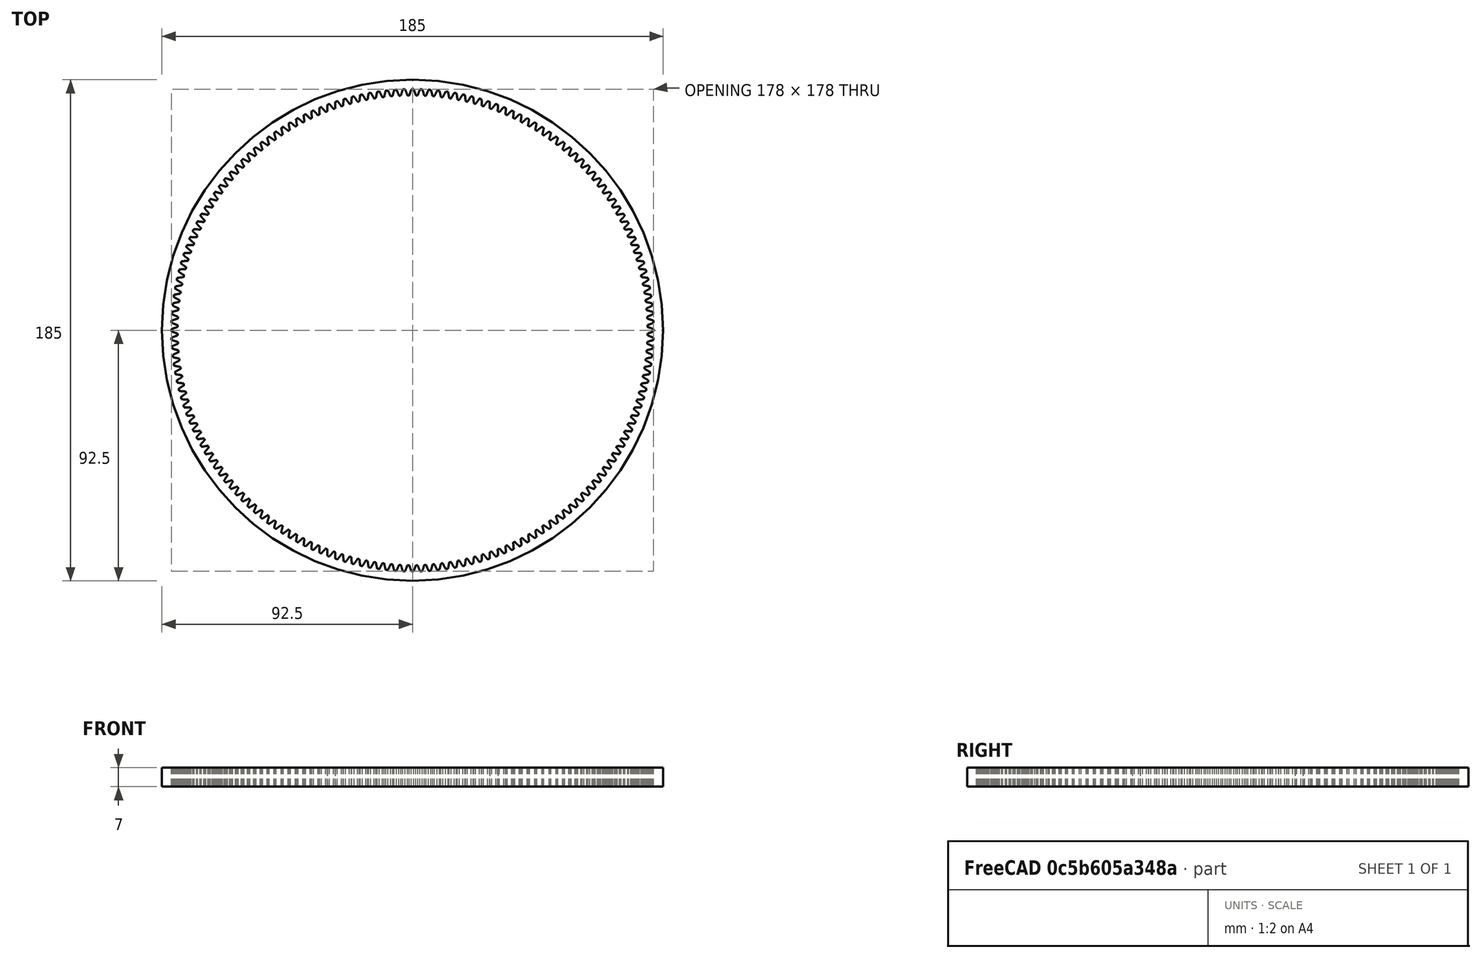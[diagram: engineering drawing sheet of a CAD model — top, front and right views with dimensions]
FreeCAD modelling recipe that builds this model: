
FCSTD DOCUMENT  (FreeCAD 0.19R24276 (Git))
Label: In_gear_t176_w7_cat_d185
License: All rights reserved
LicenseURL: http://en.wikipedia.org/wiki/All_rights_reserved
objects: PartDesign::FeaturePython×1, PartDesign::Body×1, Part::Cylinder×1, Part::Cut×1
note: 4 computed .brp shape members not serialized (recipe doc carries the construction recipe); baked Part::Feature solids carry a one-line shape summary decoded from their .brp

FEATURE [PartDesign::FeaturePython] involutegear001  # WARN: FeaturePython — macro-defined, semantics opaque (R4)
  AttacherType = Attacher::AttachEngine3D
  backlash = 0
  beta = 0
  clearance = 0.25
  da = 178
  df = 173.5
  double_helix = false
  dw = 176
  head = 0
  height = 7
  module = 1
  numpoints = 6
  pressure_angle = 20
  properties_from_tool = false
  reversed_backlash = false
  shift = 0
  simple = false
  teeth = 176
  transverse_pitch = 3.14159
  undercut = false
  version = 0.0.3
FEATURE [PartDesign::Body] Body
  Group = -> [involutegear001]
  Origin = -> Origin
  Tip = -> involutegear001
FEATURE [Part::Cylinder] Cylinder  label="Цилиндр"
  Angle = 360
  AttacherType = Attacher::AttachEngine3D
  Height = 7
  Radius = 92.5
FEATURE [Part::Cut] Cut
  Base = -> Cylinder
  Tool = -> Body
